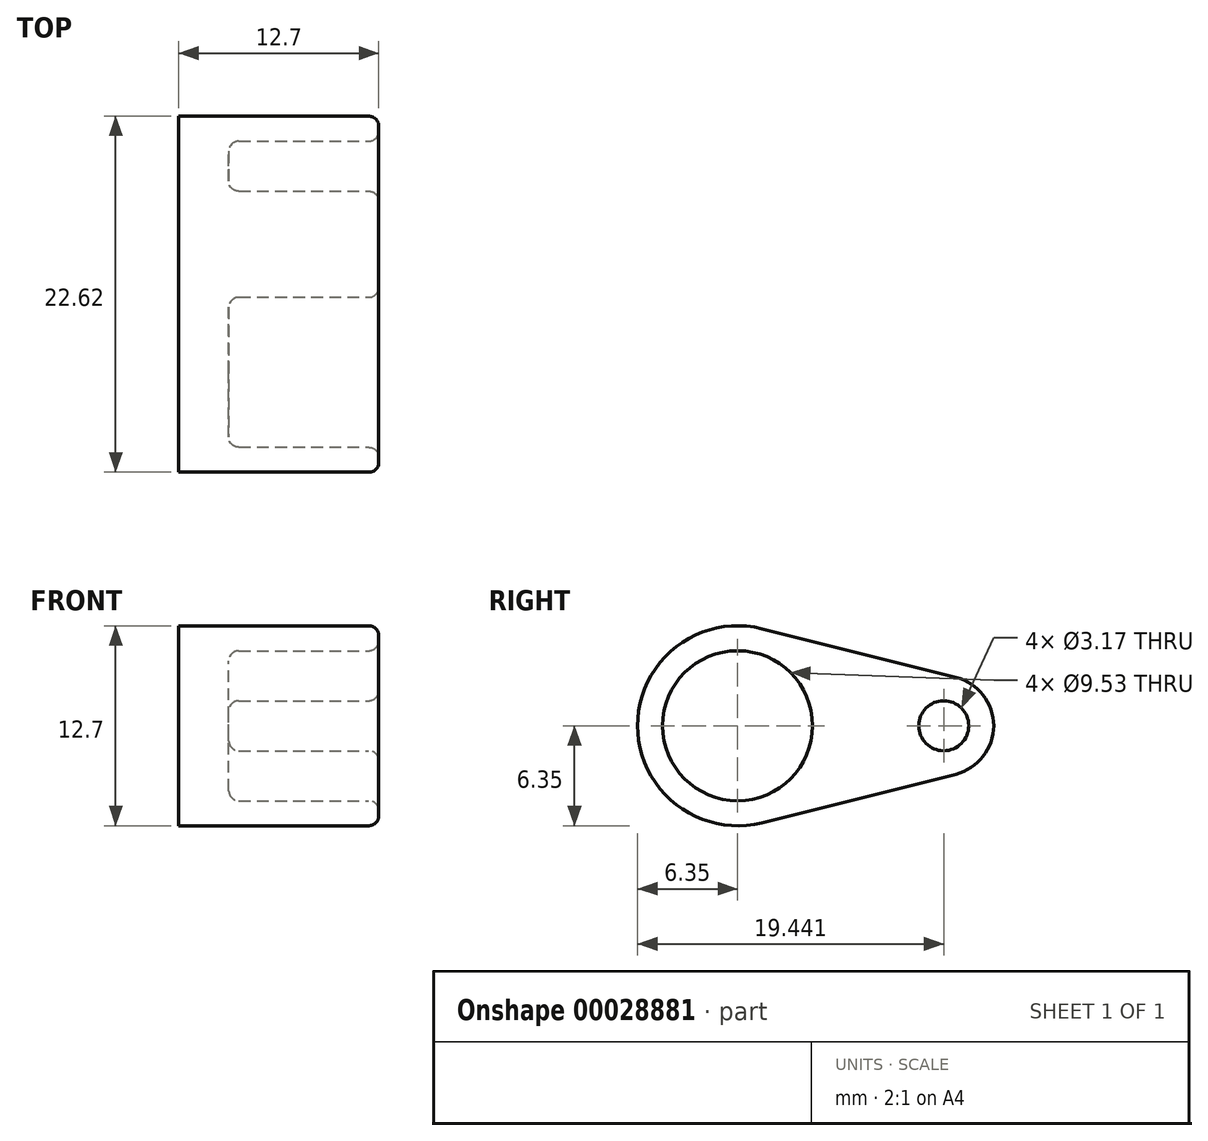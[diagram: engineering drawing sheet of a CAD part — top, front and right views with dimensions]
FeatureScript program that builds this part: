
annotation { "Feature Type Name" : "Feature", "Feature Type Description" : "" }
export const myFeature = defineFeature(function(context is Context, id is Id, definition is map)
    precondition{}
    {
        {
            var Q0;
            Q0=qCreatedBy(makeId("Right.planeOp"),FACE);
            var sketch = newSketch(context, id + "F0", { "sketchPlane" : qUnion([Q0])});
            skCircle(sketch, "E0", {"center": v(0, 0) * mm, "radius": 6.35 * mm});
            skCircle(sketch, "E1", {"center": v(13.1, 0) * mm, "radius": 3.18 * mm});
            skLineSegment(sketch, "E2", {"start": v(1.54, 6.16) * mm, "end": v(13.86, 3.08) * mm});
            skLineSegment(sketch, "E3", {"start": v(1.54, -6.16) * mm, "end": v(13.86, -3.08) * mm});
            skSolve(sketch);
        }
        {
            var Q0;
            {var subQ0=sQuery(id+"F0.wireOp",EDGE,"E0");var subQ2=makeQuery(id+"F0.imprint","INTERSECT",VERTEX,{"derivedFrom":[subQ0,sQuery(id+"F0.wireOp",EDGE,"E2")]});Q0=makeQuery(id+"F0.imprint","IMPRINT",FACE,{"disambiguationData":[TD([[makeQuery(id+"F0.imprint","IMPRINT",EDGE,{"disambiguationData":[TD([[subQ2,-1.0]])],"derivedFrom":subQ0}),1.0]])]});}
            var Q1;
            {var subQ1=sQuery(id+"F0.wireOp",EDGE,"E2");Q1=makeQuery(id+"F0.imprint","IMPRINT",FACE,{"disambiguationData":[TD([[makeQuery(id+"F0.imprint","IMPRINT",EDGE,{"derivedFrom":subQ1}),-1.0]])]});}
            var Q2;
            {var subQ0=sQuery(id+"F0.wireOp",EDGE,"E1");var subQ2=makeQuery(id+"F0.imprint","INTERSECT",VERTEX,{"derivedFrom":[subQ0,sQuery(id+"F0.wireOp",EDGE,"E2")]});Q2=makeQuery(id+"F0.imprint","IMPRINT",FACE,{"disambiguationData":[TD([[makeQuery(id+"F0.imprint","IMPRINT",EDGE,{"disambiguationData":[TD([[subQ2,-1.0]])],"derivedFrom":subQ0}),1.0]])]});}
            extrude(context, id + "F1", {"entities" : qUnion([Q0, Q1, Q2]), "depth" : 12.7 * mm});
        }
        {
            var Q0;
            Q0=makeQuery(id+"F1.opExtrude","CAP_FACE",FACE,{"disambiguationData":[OSD([sQuery(id+"F0.wireOp",EDGE,"E0"),sQuery(id+"F0.wireOp",EDGE,"E1"),sQuery(id+"F0.wireOp",EDGE,"E2"),sQuery(id+"F0.wireOp",EDGE,"E3")])],"isStart":false});
            var sketch = newSketch(context, id + "F2", { "sketchPlane" : qUnion([Q0])});
            skCircle(sketch, "E4", {"center": v(0, 0) * mm, "radius": 4.76 * mm});
            skCircle(sketch, "E5", {"center": v(13.1, 0) * mm, "radius": 1.59 * mm});
            skSolve(sketch);
        }
        {
            var Q0;
            Q0=makeQuery(id+"F2.imprint","IMPRINT",FACE,{"disambiguationData":[TD([[makeQuery(id+"F2.imprint","IMPRINT",EDGE,{"derivedFrom":sQuery(id+"F2.wireOp",EDGE,"E4")}),1.0]])]});
            var Q1;
            Q1=makeQuery(id+"F2.imprint","IMPRINT",FACE,{"disambiguationData":[TD([[makeQuery(id+"F2.imprint","IMPRINT",EDGE,{"derivedFrom":sQuery(id+"F2.wireOp",EDGE,"E5")}),1.0]])]});
            extrude(context, id + "F3", {"entities" : qUnion([Q0, Q1]), "operationType" : NewBodyOperationType.REMOVE, "oppositeDirection" : true, "depth" : 9.52 * mm});
        }
        {
            var Q0;
            Q0=makeQuery(id+"F1.opExtrude","CAP_FACE",FACE,{"disambiguationData":[OSD([sQuery(id+"F0.wireOp",EDGE,"E0"),sQuery(id+"F0.wireOp",EDGE,"E1"),sQuery(id+"F0.wireOp",EDGE,"E2"),sQuery(id+"F0.wireOp",EDGE,"E3")])],"isStart":false});
            var Q1;
            Q1=makeQuery(id+"F3.boolean.opBoolean","COPY",EDGE,{"derivedFrom":makeQuery(id+"F3.opExtrude","CAP_EDGE",EDGE,{"disambiguationData":[OSD([sQuery(id+"F2.wireOp",EDGE,"E4")])],"isStart":false})});
            var Q2;
            Q2=makeQuery(id+"F3.boolean.opBoolean","COPY",EDGE,{"derivedFrom":makeQuery(id+"F3.opExtrude","CAP_EDGE",EDGE,{"disambiguationData":[OSD([sQuery(id+"F2.wireOp",EDGE,"E5")])],"isStart":true})});
            var Q3;
            Q3=makeQuery(id+"F3.boolean.opBoolean","COPY",EDGE,{"derivedFrom":makeQuery(id+"F3.opExtrude","CAP_EDGE",EDGE,{"disambiguationData":[OSD([sQuery(id+"F2.wireOp",EDGE,"E5")])],"isStart":false})});
            fillet(context, id + "F4", {"entities" : qUnion([Q0, Q1, Q2, Q3]), "radius" : 0.64 * mm, "tangentPropagation" : true, "allowEdgeOverflow" : false});
        }
    });
